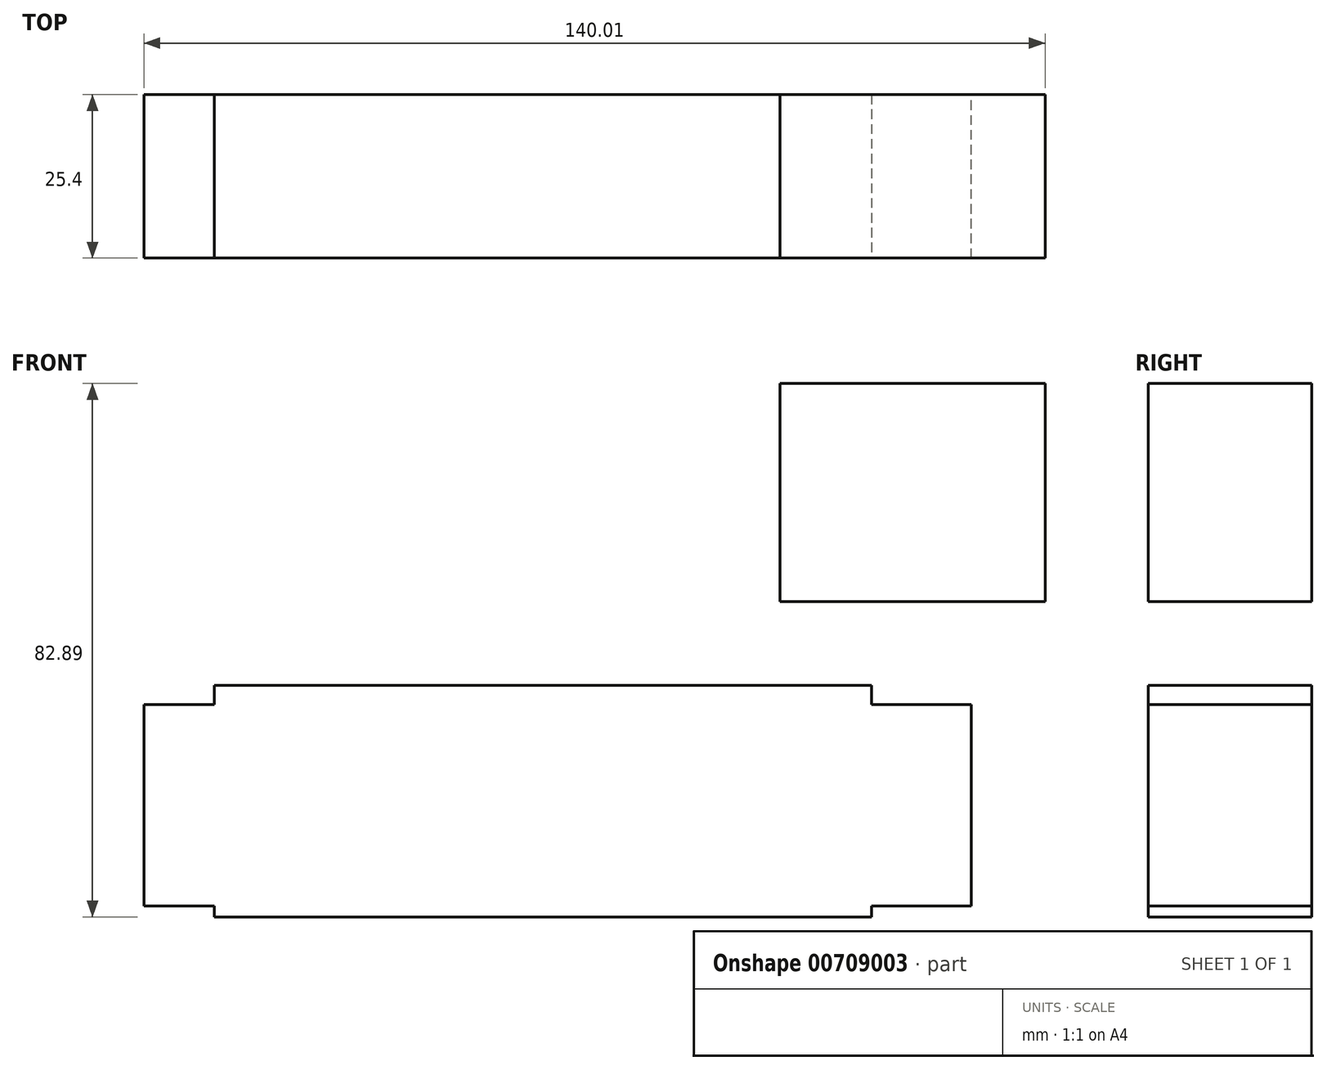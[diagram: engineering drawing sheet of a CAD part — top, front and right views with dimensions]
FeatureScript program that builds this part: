
annotation { "Feature Type Name" : "Feature", "Feature Type Description" : "" }
export const myFeature = defineFeature(function(context is Context, id is Id, definition is map)
    precondition{}
    {
        {
            var Q0;
            Q0=qCreatedBy(makeId("Front.planeOp"),FACE);
            var sketch = newSketch(context, id + "F0", { "sketchPlane" : qUnion([Q0])});
            skSolve(sketch);
        }
        {
            var Q0;
            Q0=qCreatedBy(makeId("Front.planeOp"),FACE);
            var sketch = newSketch(context, id + "F1", { "sketchPlane" : qUnion([Q0])});
            skSolve(sketch);
        }
        {
            var Q0;
            Q0=qCreatedBy(makeId("Front.planeOp"),FACE);
            var sketch = newSketch(context, id + "F2", { "sketchPlane" : qUnion([Q0])});
            skLineSegment(sketch, "E0.bottom", {"start": v(-64.46, 13.96) * mm, "end": v(64.07, 13.96) * mm});
            skLineSegment(sketch, "E0.top", {"start": v(-64.46, -17.33) * mm, "end": v(64.07, -17.33) * mm});
            skLineSegment(sketch, "E0.left", {"start": v(-64.46, 13.96) * mm, "end": v(-64.46, -17.33) * mm});
            skLineSegment(sketch, "E0.right", {"start": v(64.07, 13.96) * mm, "end": v(64.07, -17.33) * mm});
            skLineSegment(sketch, "E1.bottom", {"start": v(34.36, 63.87) * mm, "end": v(75.55, 63.87) * mm});
            skLineSegment(sketch, "E1.top", {"start": v(34.36, 30) * mm, "end": v(75.55, 30) * mm});
            skLineSegment(sketch, "E1.left", {"start": v(34.36, 63.87) * mm, "end": v(34.36, 30) * mm});
            skLineSegment(sketch, "E1.right", {"start": v(75.55, 63.87) * mm, "end": v(75.55, 30) * mm});
            skLineSegment(sketch, "E2", {"start": v(64.07, 13.96) * mm, "end": v(64.07, 35.75) * mm});
            skSolve(sketch);
        }
        {
            var Q0;
            Q0=qCreatedBy(makeId("Front.planeOp"),FACE);
            var sketch = newSketch(context, id + "F3", { "sketchPlane" : qUnion([Q0])});
            skLineSegment(sketch, "E3.bottom", {"start": v(-53.56, 16.97) * mm, "end": v(48.58, 16.97) * mm});
            skLineSegment(sketch, "E3.top", {"start": v(-53.56, -19.02) * mm, "end": v(48.58, -19.02) * mm});
            skLineSegment(sketch, "E3.left", {"start": v(-53.56, 16.97) * mm, "end": v(-53.56, -19.02) * mm});
            skLineSegment(sketch, "E3.right", {"start": v(48.58, 16.97) * mm, "end": v(48.58, -19.02) * mm});
            skLineSegment(sketch, "E4.bottom", {"start": v(86.04, 113.63) * mm, "end": v(129.65, 113.63) * mm});
            skLineSegment(sketch, "E4.top", {"start": v(86.04, 56.48) * mm, "end": v(129.65, 56.48) * mm});
            skLineSegment(sketch, "E4.left", {"start": v(86.04, 113.63) * mm, "end": v(86.04, 56.48) * mm});
            skLineSegment(sketch, "E4.right", {"start": v(129.65, 113.63) * mm, "end": v(129.65, 56.48) * mm});
            skLineSegment(sketch, "E5", {"start": v(48.58, 16.97) * mm, "end": v(48.58, 50.34) * mm});
            skArc(sketch, "E6", {"start": v(72.29, 50.34) * mm, "mid": v(60.43, 62.19) * mm, "end": v(48.58, 50.34) * mm});
            skLineSegment(sketch, "E7", {"start": v(72.29, 50.34) * mm, "end": v(99.8, 50.34) * mm});
            skLineSegment(sketch, "E8.0", {"start": v(81.7, 63.5) * mm, "end": v(99.8, 63.5) * mm});
            skArc(sketch, "E8.1", {"start": v(81.7, 63.5) * mm, "mid": v(53.59, 74.4) * mm, "end": v(35.41, 50.34) * mm});
            skLineSegment(sketch, "E8.2", {"start": v(35.41, 16.97) * mm, "end": v(35.41, 50.34) * mm});
            skLineSegment(sketch, "E9", {"start": v(99.8, 50.34) * mm, "end": v(99.8, 63.5) * mm});
            skSolve(sketch);
        }
        {
            var Q0;
            Q0=qCreatedBy(makeId("Front.planeOp"),FACE);
            var sketch = newSketch(context, id + "F4", { "sketchPlane" : qUnion([Q0])});
            skFitSpline(sketch, "E10", {"points": [v(-52.97, 17.27) * mm, v(35.41, 50.92) * mm], "startDerivative": vector(88.38, 33.66) * mm, "endDerivative": vector(88.38, 33.66) * mm});
            skSolve(sketch);
        }
        {
            var Q0;
            Q0=makeQuery(id+"F3.imprint","IMPRINT",FACE,{"disambiguationData":[TD([[makeQuery(id+"F3.imprint","IMPRINT",EDGE,{"derivedFrom":sQuery(id+"F3.wireOp",EDGE,"E3.top")}),1.0]])]});
            extrude(context, id + "F5", {"entities" : qUnion([Q0]), "endBound" : BoundingType.SYMMETRIC, "depth" : 25.4 * mm, "offsetDistance" : 25.4 * mm});
        }
        {
            var Q0;
            Q0=sQuery(id+"F4.wireOp",EDGE,"E10");
            extrude(context, id + "F6", {"bodyType" : ToolBodyType.SURFACE, "surfaceEntities" : qUnion([Q0]), "endBound" : BoundingType.SYMMETRIC, "depth" : 12.7 * mm, "offsetDistance" : 25.4 * mm});
        }
        {
            var Q0;
            Q0 = qSketchRegion(id + "F0", true);
            var Q1;
            Q1 = qSketchRegion(id + "F1", true);
            var Q2;
            Q2 = qSketchRegion(id + "F2", true);
            extrude(context, id + "F7", {"entities" : qUnion([Q0, Q1, Q2]), "operationType" : NewBodyOperationType.ADD, "endBound" : BoundingType.SYMMETRIC, "depth" : 25.4 * mm, "offsetDistance" : 25.4 * mm});
        }
    });
